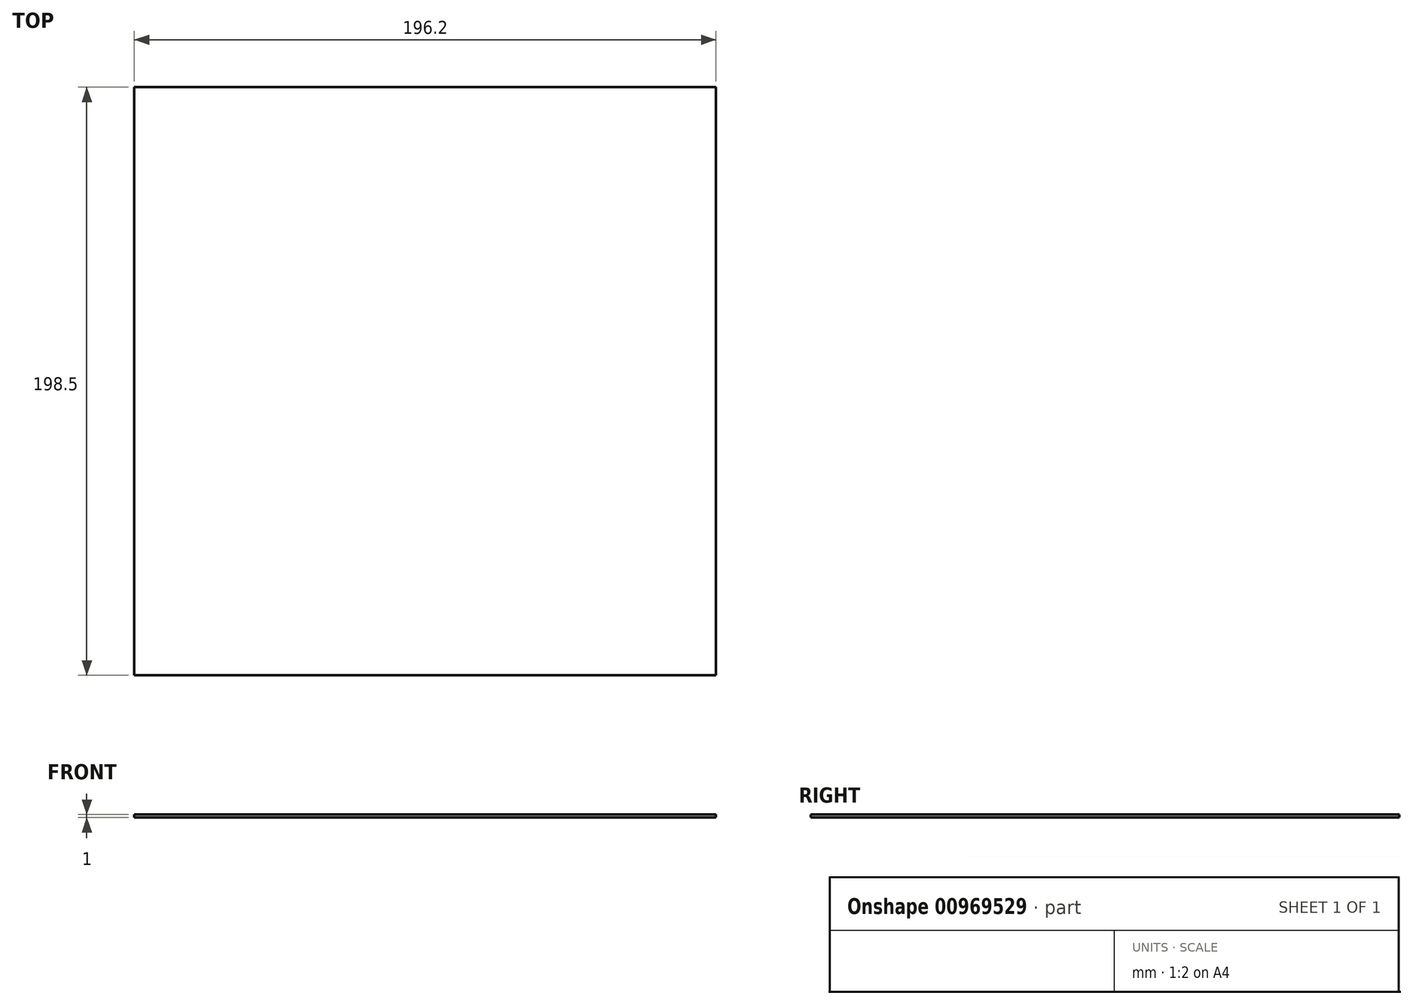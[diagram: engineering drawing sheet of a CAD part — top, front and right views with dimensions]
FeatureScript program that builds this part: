
annotation { "Feature Type Name" : "Feature", "Feature Type Description" : "" }
export const myFeature = defineFeature(function(context is Context, id is Id, definition is map)
    precondition{}
    {
        {
            var Q0;
            Q0=qCreatedBy(makeId("Top.planeOp"),FACE);
            var sketch = newSketch(context, id + "F0", { "sketchPlane" : qUnion([Q0])});
            skLineSegment(sketch, "E0.bottom", {"start": v(-98.1, 99.25) * mm, "end": v(98.1, 99.25) * mm});
            skLineSegment(sketch, "E0.top", {"start": v(-98.1, -99.25) * mm, "end": v(98.1, -99.25) * mm});
            skLineSegment(sketch, "E0.left", {"start": v(-98.1, 99.25) * mm, "end": v(-98.1, -99.25) * mm});
            skLineSegment(sketch, "E0.right", {"start": v(98.1, 99.25) * mm, "end": v(98.1, -99.25) * mm});
            skPoint(sketch, "E0.middle", {"position": v(0, 0) * mm});
            skSolve(sketch);
        }
        {
            var Q0;
            Q0=makeQuery(id+"F0.imprint","IMPRINT",FACE,{"disambiguationData":[TD([[makeQuery(id+"F0.imprint","IMPRINT",EDGE,{"derivedFrom":sQuery(id+"F0.wireOp",EDGE,"E0.bottom")}),-1.0]])]});
            extrude(context, id + "F1", {"entities" : qUnion([Q0]), "depth" : 1 * mm, "offsetDistance" : 25 * mm});
        }
    });
